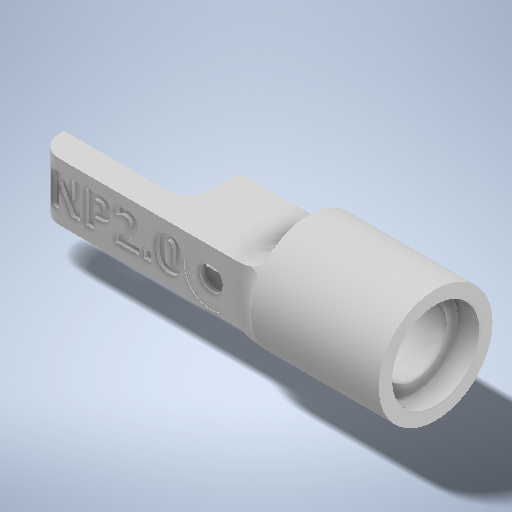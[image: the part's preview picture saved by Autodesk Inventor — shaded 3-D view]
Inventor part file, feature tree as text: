
AUTODESK INVENTOR PART (.ipt)
format: ipt  version: 2025 (Build 290162000, 162)  size: 678,400 bytes
history: native  units: mm
features: extrude x12, reference x8, fillet x5, other x3, sketch x2, emboss x1, projected_geometry x1
ambient origin geometry x8: Origin, YZ Plane, XZ Plane, XY Plane, X Axis, Y Axis, Z Axis, Center Point
bodies: Solid1 (feature_tree)
feature tree (32):
  extrude  "Extrusion1"  Depth=1.0mm
  extrude  "Extrusion2"  Depth=0.3mm
  extrude  "Extrusion3"  Depth=0.3mm TaperAngle=0.0deg
  extrude  "Extrusion4"  Depth=0.3mm TaperAngle=0.0deg
  fillet  "Fillet1"  Radius=1.1mm
  extrude  "Extrusion5"  Depth=0.3mm TaperAngle=0.0deg
  fillet  "Fillet2"  Radius=1.0mm
  fillet  "Fillet3"  Radius=1.0mm
  extrude  "Extrusion6"  Depth=0.3mm
  extrude  "Extrusion7"  Depth=0.3mm
  extrude  "Extrusion8"  Depth=0.3mm TaperAngle=0.0deg
  extrude  "Extrusion9"  Depth=0.3mm
  extrude  "Extrusion10"  Depth=0.3mm
  extrude  "Extrusion11"  Depth=0.3mm
  emboss  "Emboss1"
  extrude  "Extrusion12"  Depth=0.3mm
  fillet  "Fillet4"  Radius=4.4mm
  fillet  "Fillet5"  Radius=10.704mm
  reference  "Reference1"
  reference  "Reference2"
  reference  "Reference3"
  reference  "Reference4"
  reference  "Reference5"
  reference  "Reference6"
  reference  "Reference7"
  projected_geometry  "Projected Loop1"
  sketch  "Sketch13"  dims[d0=7.0mm d1=1.0mm]
  sketch  "Sketch14"  dims[d2=1.0mm d3=21.0mm d4=1.7mm d5=0.0mm d9=1.0mm d10=0.0mm d11=1.1mm d12=5.8mm d13=0.0mm d14=1.0mm d15=1.0mm d16=1.0mm d17=1.0mm d18=6.9mm d19=0.0mm d20=2.0mm d21=7.5mm d22=5.4mm d23=2.7mm d24=4.4mm d25=10.704mm d26=12.0mm d27=0.0mm d28=3.0mm d29=2.0mm d30=8.2mm d31=2.0mm d32=0.0mm d33=6.1mm d34=7.0mm d35=0.0mm d36=3.0mm d37=8.0mm d38=0.0mm d40=5.0mm d41=20.0mm d42=3.5mm d43=0.0mm d44=0.0mm d45=2.2mm d46=3.4mm d47=7.5mm d48=3.75mm d49=1.7mm d50=20.0mm d51=0.0mm d52=5.0mm d53=0.05mm d54=0.0mm d55=0.3mm d56=0.0mm d58=1.5mm d59=0.0mm d60=0.14mm d61=0.14mm d62=0.3mm d63=0.3mm d64=1.19mm d65=1.19mm d66=3.2mm d57=0.5mm]
  reference  "Reference8"
  parser-record x1  (decoder bookkeeping rows leaked as tree rows — omitted from the tree; the rows remain in map.json)
  other  "np2_full_assembly.iam"
  other  "np2_main_chassis:1"
note: 1 file-system path scrubbed to <path> (originals preserved in map.json)
